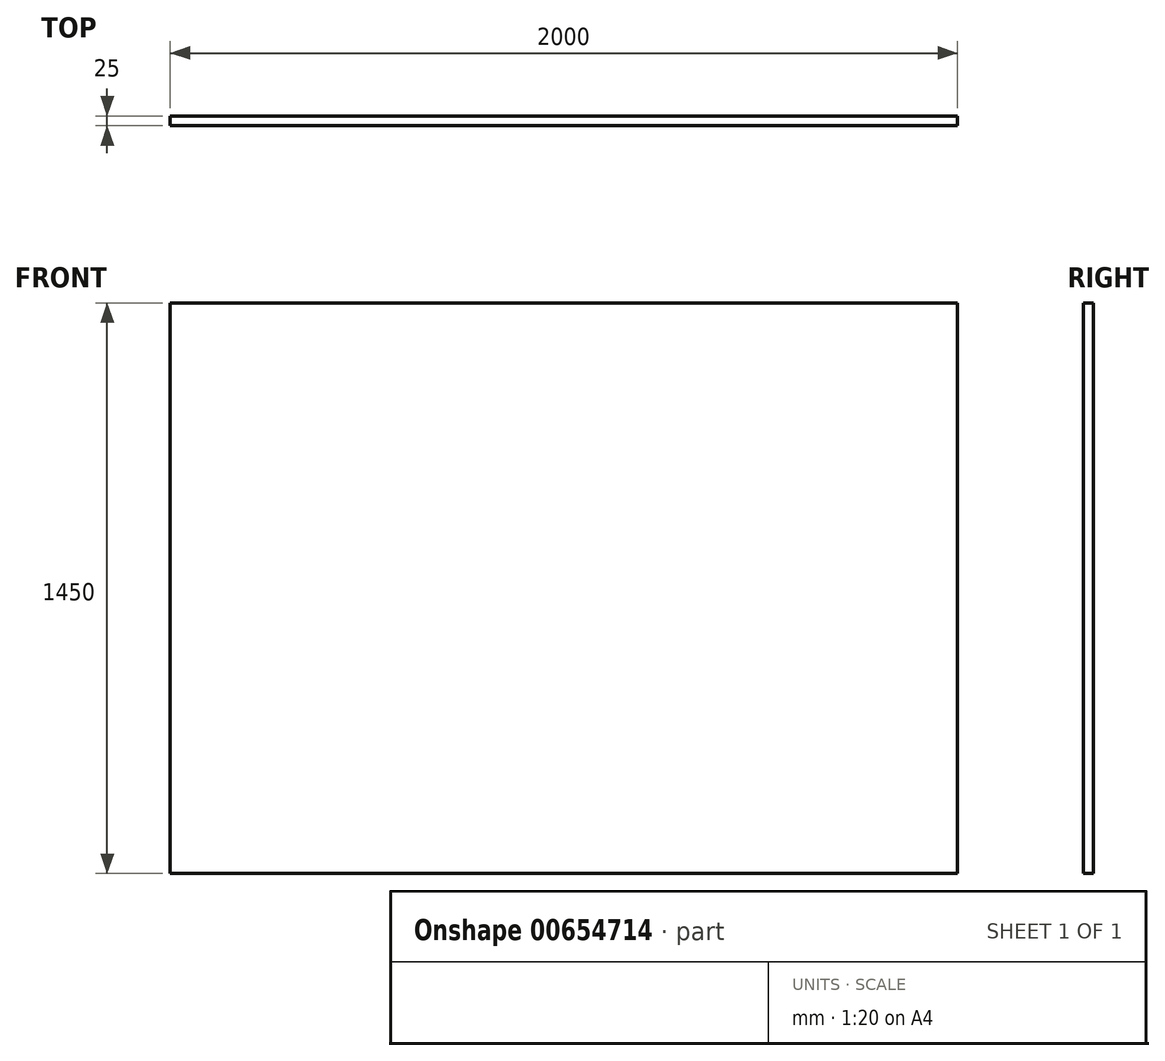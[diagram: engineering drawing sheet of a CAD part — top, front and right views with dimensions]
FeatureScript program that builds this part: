
annotation { "Feature Type Name" : "Feature", "Feature Type Description" : "" }
export const myFeature = defineFeature(function(context is Context, id is Id, definition is map)
    precondition{}
    {
        {
            var Q0;
            Q0=qCreatedBy(makeId("Front.planeOp"),FACE);
            var sketch = newSketch(context, id + "F0", { "sketchPlane" : qUnion([Q0])});
            skLineSegment(sketch, "E0.bottom", {"start": v(-924.66, 513.3) * mm, "end": v(1075.34, 513.3) * mm});
            skLineSegment(sketch, "E0.top", {"start": v(-924.66, -936.7) * mm, "end": v(1075.34, -936.7) * mm});
            skLineSegment(sketch, "E0.left", {"start": v(-924.66, 513.3) * mm, "end": v(-924.66, -936.7) * mm});
            skLineSegment(sketch, "E0.right", {"start": v(1075.34, 513.3) * mm, "end": v(1075.34, -936.7) * mm});
            skSolve(sketch);
        }
        {
            var Q0;
            Q0 = qSketchRegion(id + "F0", true);
            extrude(context, id + "F1", {"entities" : qUnion([Q0]), "depth" : 25 * mm, "offsetDistance" : 25 * mm});
        }
    });
